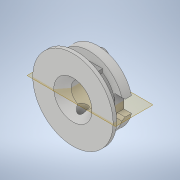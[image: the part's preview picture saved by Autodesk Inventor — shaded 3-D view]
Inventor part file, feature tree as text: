
AUTODESK INVENTOR PART (.ipt)
format: ipt  version: 2020.4 (Build 244396010, 396A)  size: 201,216 bytes
history: native  units: mm
features: extrude x2, sketch x2, plane x1, mirror x1, imported_body x1
ambient origin geometry x8: Origin, YZ Plane, XZ Plane, XY Plane, X Axis, Y Axis, Z Axis, Center Point
bodies: Solid1 (feature_tree)
feature tree (7):
  extrude  "Extrusion1"  Depth=3.5mm
  extrude  "Extrusion2"  Depth=3.0mm TaperAngle=0.0deg
  plane  "Work Plane1"
  mirror  "Mirror1"
  sketch  "Sketch1"  dims[d0=4.2mm d1=3.5mm]
  sketch  "Sketch2"  dims[d2=4.0mm d3=0.0mm d5=3.0mm d6=0.0mm d7=3.5mm d8=2.0mm]
  imported_body  "Base1"
